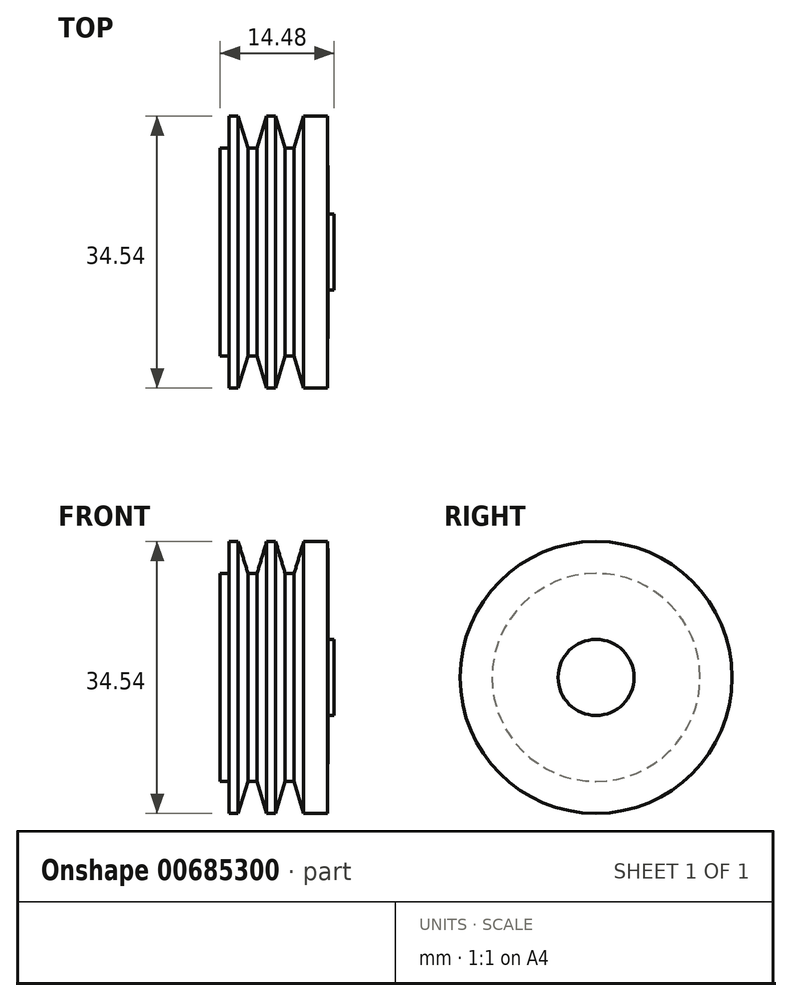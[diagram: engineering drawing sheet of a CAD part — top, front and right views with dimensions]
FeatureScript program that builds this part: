
annotation { "Feature Type Name" : "Feature", "Feature Type Description" : "" }
export const myFeature = defineFeature(function(context is Context, id is Id, definition is map)
    precondition{}
    {
        {
            var Q0;
            Q0=qCreatedBy(makeId("Front.planeOp"),FACE);
            var sketch = newSketch(context, id + "F0", { "sketchPlane" : qUnion([Q0])});
            skLineSegment(sketch, "E0", {"start": v(-9.4, 0) * mm, "end": v(-9.4, 13.2) * mm});
            skLineSegment(sketch, "E1", {"start": v(-9.4, 13.2) * mm, "end": v(-8.26, 13.2) * mm});
            skLineSegment(sketch, "E2", {"start": v(-8.26, 13.2) * mm, "end": v(-8.26, 17.27) * mm});
            skLineSegment(sketch, "E3", {"start": v(-8.26, 17.27) * mm, "end": v(-7.11, 17.27) * mm});
            skLineSegment(sketch, "E4", {"start": v(-7.11, 17.27) * mm, "end": v(-5.86, 13.2) * mm});
            skLineSegment(sketch, "E5", {"start": v(-5.86, 13.2) * mm, "end": v(-4.72, 13.2) * mm});
            skLineSegment(sketch, "E6", {"start": v(-4.72, 13.2) * mm, "end": v(-3.5, 17.27) * mm});
            skLineSegment(sketch, "E7", {"start": v(-3.5, 17.27) * mm, "end": v(-2.36, 17.27) * mm});
            skLineSegment(sketch, "E8", {"start": v(-2.36, 17.27) * mm, "end": v(-1.14, 13.2) * mm});
            skLineSegment(sketch, "E9", {"start": v(-1.14, 13.2) * mm, "end": v(0, 13.2) * mm});
            skLineSegment(sketch, "E10", {"start": v(0, 13.2) * mm, "end": v(1.22, 17.27) * mm});
            skLineSegment(sketch, "E11", {"start": v(1.22, 17.27) * mm, "end": v(4.26, 17.27) * mm});
            skLineSegment(sketch, "E12", {"start": v(4.26, 17.27) * mm, "end": v(4.3, 4.82) * mm});
            skLineSegment(sketch, "E13", {"start": v(4.3, 4.82) * mm, "end": v(5.06, 4.83) * mm});
            skLineSegment(sketch, "E14", {"start": v(5.06, 4.83) * mm, "end": v(5.08, 0) * mm});
            skPoint(sketch, "E15.start.orphan", {"position": v(4.32, 0) * mm});
            skLineSegment(sketch, "E16", {"start": v(-9.4, 0) * mm, "end": v(5.08, 0) * mm});
            skSolve(sketch);
        }
        {
            var Q0;
            Q0=makeQuery(id+"F0.imprint","IMPRINT",FACE,{"disambiguationData":[TD([[makeQuery(id+"F0.imprint","IMPRINT",EDGE,{"derivedFrom":sQuery(id+"F0.wireOp",EDGE,"E0")}),-1.0]])]});
            var Q1;
            Q1=sQuery(id+"F0.wireOp",EDGE,"E16");
            revolve(context, id + "F1", {"entities" : qUnion([Q0]), "axis" : qUnion([Q1]), "revolveType" : RevolveType.FULL});
        }
    });
